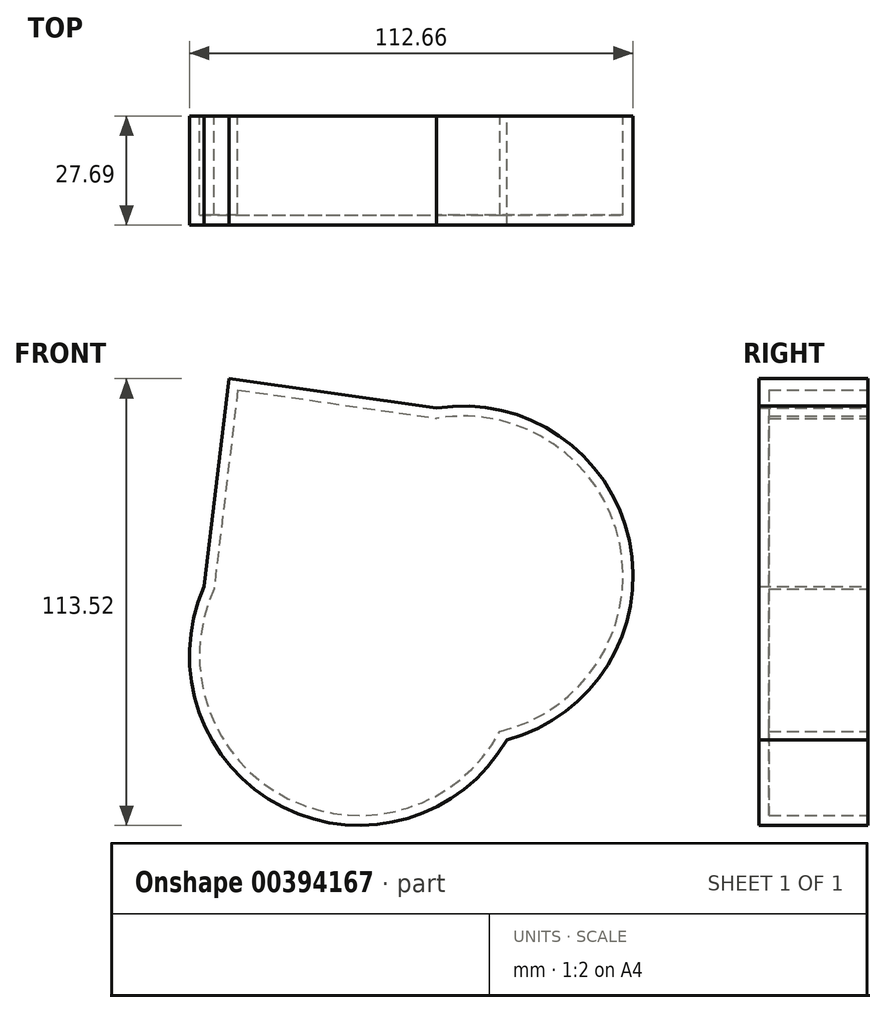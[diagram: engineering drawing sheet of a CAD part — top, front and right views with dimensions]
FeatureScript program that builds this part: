
annotation { "Feature Type Name" : "Feature", "Feature Type Description" : "" }
export const myFeature = defineFeature(function(context is Context, id is Id, definition is map)
    precondition{}
    {
        {
            var Q0;
            Q0=qCreatedBy(makeId("Front.planeOp"),FACE);
            var sketch = newSketch(context, id + "F0", { "sketchPlane" : qUnion([Q0])});
            skLineSegment(sketch, "E0", {"start": v(-37.64, 47.5) * mm, "end": v(32.91, -44.34) * mm});
            skLineSegment(sketch, "E1", {"start": v(-37.64, 47.5) * mm, "end": v(-43.95, -5.32) * mm});
            skArc(sketch, "E2", {"start": v(-43.95, -5.32) * mm, "mid": v(-24.06, -61.36) * mm, "end": v(32.91, -44.34) * mm});
            skSolve(sketch);
        }
        {
            var Q0;
            Q0=makeQuery(id+"F0.imprint","IMPRINT",FACE,{"disambiguationData":[TD([[makeQuery(id+"F0.imprint","IMPRINT",EDGE,{"derivedFrom":sQuery(id+"F0.wireOp",EDGE,"E0")}),-1.0]])]});
            extrude(context, id + "F1", {"entities" : qUnion([Q0]), "depth" : 27.7 * mm});
        }
        {
            var Q0;
            Q0=makeQuery(id+"F1.opExtrude","SWEPT_BODY",BODY,{"disambiguationData":[OSD([sQuery(id+"F0.wireOp",EDGE,"E0"),sQuery(id+"F0.wireOp",EDGE,"E1"),sQuery(id+"F0.wireOp",EDGE,"E2")])]});
            var Q1;
            Q1=makeQuery(id+"F1.opExtrude","SWEPT_FACE",FACE,{"disambiguationData":[OSD([sQuery(id+"F0.wireOp",EDGE,"E0")])]});
            mirror(context, id + "F2", {"operationType" : NewBodyOperationType.ADD, "entities" : qUnion([Q0]), "mirrorPlane" : qUnion([Q1])});
        }
        {
            var Q0;
            {var subQ0=makeQuery(id+"F1.opExtrude","CAP_FACE",FACE,{"disambiguationData":[OSD([sQuery(id+"F0.wireOp",EDGE,"E0"),sQuery(id+"F0.wireOp",EDGE,"E1"),sQuery(id+"F0.wireOp",EDGE,"E2")])],"isStart":true});Q0=makeQuery(id+"F2.boolean.opBoolean","MERGE",FACE,{"derivedFrom":[subQ0,makeQuery(id+"F2.opPattern","COPY",FACE,{"derivedFrom":subQ0,"instanceName":"1"})]});}
            shell(context, id + "F3", {"entities" : qUnion([Q0]), "thickness" : 2.54 * mm});
        }
    });
